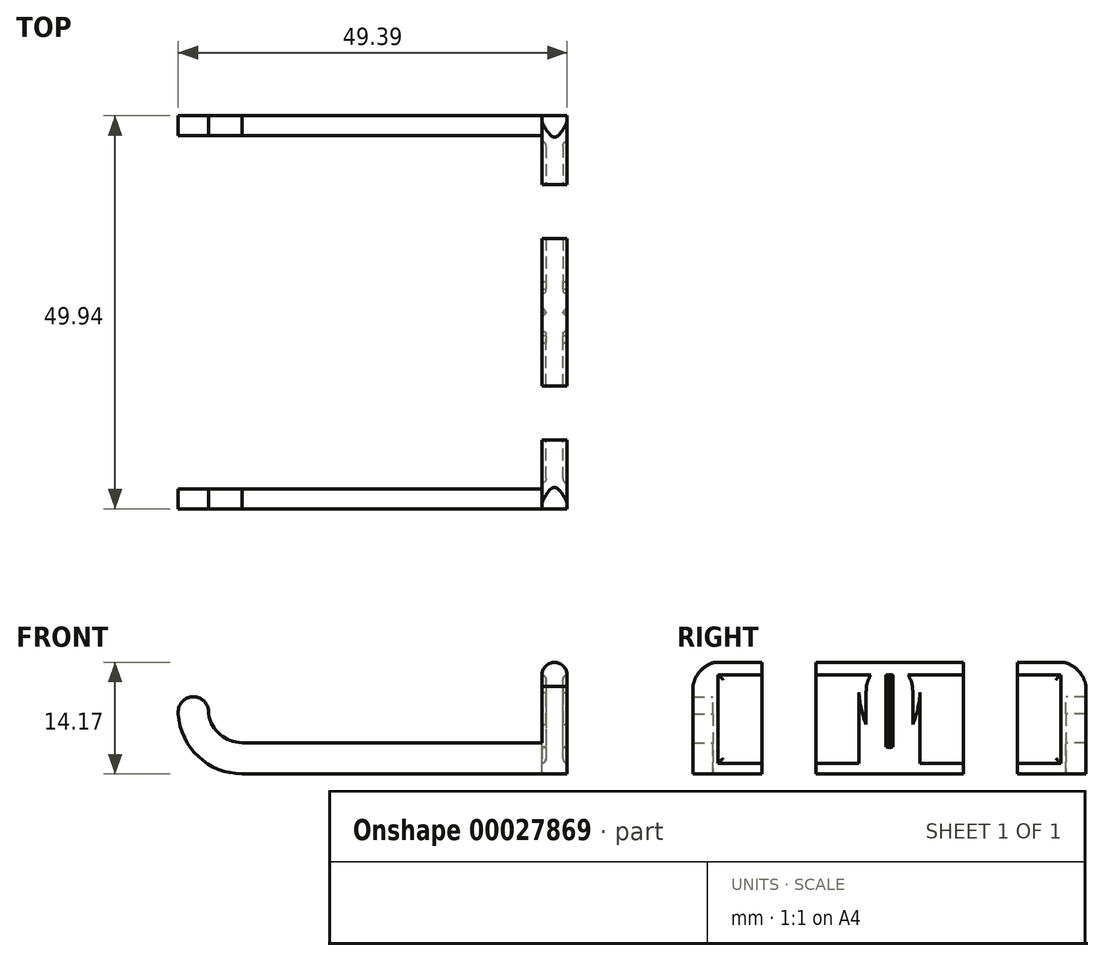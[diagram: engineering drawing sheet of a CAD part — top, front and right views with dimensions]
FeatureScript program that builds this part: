
annotation { "Feature Type Name" : "Feature", "Feature Type Description" : "" }
export const myFeature = defineFeature(function(context is Context, id is Id, definition is map)
    precondition{}
    {
        {
            var Q0;
            Q0=qCreatedBy(makeId("Front.planeOp"),FACE);
            var sketch = newSketch(context, id + "F0", { "sketchPlane" : qUnion([Q0])});
            skLineSegment(sketch, "E0", {"start": v(-12.84, 0) * mm, "end": v(25.26, 0) * mm});
            skArc(sketch, "E1", {"start": v(-20.94, 7.59) * mm, "mid": v(-18.39, 2.2) * mm, "end": v(-12.84, 0) * mm});
            skArc(sketch, "E2", {"start": v(-17.1, 7.59) * mm, "mid": v(-19.02, 9.79) * mm, "end": v(-20.94, 7.59) * mm});
            skArc(sketch, "E3", {"start": v(-17.1, 7.59) * mm, "mid": v(-15.62, 5) * mm, "end": v(-12.84, 3.94) * mm});
            skLineSegment(sketch, "E4", {"start": v(-12.84, 3.94) * mm, "end": v(25.26, 3.94) * mm});
            skLineSegment(sketch, "E5", {"start": v(25.26, 3.94) * mm, "end": v(25.26, 12.58) * mm});
            skLineSegment(sketch, "E6", {"start": v(25.26, 0) * mm, "end": v(28.43, 0) * mm});
            skLineSegment(sketch, "E7", {"start": v(28.43, 0) * mm, "end": v(28.43, 12.58) * mm});
            skArc(sketch, "E8", {"start": v(28.43, 12.58) * mm, "mid": v(26.85, 14.17) * mm, "end": v(25.26, 12.58) * mm});
            skLineSegment(sketch, "E9", {"start": v(25.26, 3.94) * mm, "end": v(25.26, 0) * mm});
            skSolve(sketch);
        }
        {
            var Q0;
            Q0=makeQuery(id+"F0.imprint","IMPRINT",FACE,{"disambiguationData":[TD([[makeQuery(id+"F0.imprint","IMPRINT",EDGE,{"derivedFrom":sQuery(id+"F0.wireOp",EDGE,"E0")}),1.0]])]});
            var Q1;
            Q1=makeQuery(id+"F0.imprint","IMPRINT",FACE,{"disambiguationData":[TD([[makeQuery(id+"F0.imprint","IMPRINT",EDGE,{"derivedFrom":sQuery(id+"F0.wireOp",EDGE,"E5")}),-1.0]])]});
            extrude(context, id + "F1", {"entities" : qUnion([Q0, Q1]), "depth" : 2.54 * mm});
        }
        {
            var Q0;
            Q0=makeQuery(id+"F0.imprint","IMPRINT",FACE,{"disambiguationData":[TD([[makeQuery(id+"F0.imprint","IMPRINT",EDGE,{"derivedFrom":sQuery(id+"F0.wireOp",EDGE,"E5")}),-1.0]])]});
            extrude(context, id + "F2", {"entities" : qUnion([Q0]), "oppositeDirection" : true, "depth" : 25.4 * mm});
        }
        {
            var Q0;
            Q0=makeQuery(id+"F2.opExtrude","SWEPT_FACE",FACE,{"disambiguationData":[OSD([sQuery(id+"F0.wireOp",EDGE,"E7")])]});
            var sketch = newSketch(context, id + "F3", { "sketchPlane" : qUnion([Q0])});
            skArc(sketch, "E10", {"start": v(1.73, 14.27) * mm, "mid": v(-1.39, 13.27) * mm, "end": v(-2.58, 10.23) * mm});
            skLineSegment(sketch, "E11", {"start": v(-2.58, 10.23) * mm, "end": v(-2.58, 14.27) * mm});
            skLineSegment(sketch, "E12", {"start": v(1.73, 14.27) * mm, "end": v(-2.58, 14.27) * mm});
            skArc(sketch, "E13.MirrorCS", {"start": v(21.09, 14.27) * mm, "mid": v(23.89, 13.54) * mm, "end": v(25.37, 11.05) * mm});
            skLineSegment(sketch, "E14.MirrorCS", {"start": v(21.09, 14.27) * mm, "end": v(25.4, 14.27) * mm});
            skLineSegment(sketch, "E15.bottom", {"start": v(0.67, 12.58) * mm, "end": v(22.89, 12.58) * mm});
            skLineSegment(sketch, "E15.top", {"start": v(0.67, 1.34) * mm, "end": v(22.89, 1.34) * mm});
            skLineSegment(sketch, "E15.right", {"start": v(22.89, 12.58) * mm, "end": v(22.89, 1.34) * mm});
            skArc(sketch, "E16", {"start": v(25.4, 12.3) * mm, "mid": v(25.4, 12.27) * mm, "end": v(25.4, 12.23) * mm});
            skPoint(sketch, "E17.orphan", {"position": v(29.58, 2) * mm});
            skLineSegment(sketch, "E18", {"start": v(25.4, 0) * mm, "end": v(29.29, 0) * mm});
            skLineSegment(sketch, "E19", {"start": v(29.29, 0) * mm, "end": v(29.29, 1.92) * mm});
            skLineSegment(sketch, "E20", {"start": v(0.67, 12.58) * mm, "end": v(0.67, 1.34) * mm});
            skLineSegment(sketch, "E21", {"start": v(25.4, 10.28) * mm, "end": v(25.4, 14.27) * mm});
            skArc(sketch, "E22.trimOffspring", {"start": v(25.37, 11.05) * mm, "mid": v(25.88, 7.57) * mm, "end": v(27.27, 4.34) * mm});
            skArc(sketch, "E23.trimOffspring", {"start": v(25.4, 10.72) * mm, "mid": v(25.4, 10.5) * mm, "end": v(25.4, 10.28) * mm});
            skArc(sketch, "E24", {"start": v(27.27, 4.34) * mm, "mid": v(28.2, 3.7) * mm, "end": v(29.29, 3.34) * mm});
            skLineSegment(sketch, "E25", {"start": v(29.29, 1.92) * mm, "end": v(29.29, 3.34) * mm});
            skPoint(sketch, "E26.start.orphan", {"position": v(29, 2) * mm});
            skSolve(sketch);
        }
        {
            var Q0;
            {var subQ0=sQuery(id+"F3.wireOp",EDGE,"E12");var subQ1=sQuery(id+"F3.wireOp",EDGE,"E10");var subQ2=makeQuery(id+"F3.imprint","INTERSECT",VERTEX,{"disambiguationData":[OD(1.0)],"derivedFrom":[subQ1,subQ0]});Q0=makeQuery(id+"F3.imprint","IMPRINT",FACE,{"disambiguationData":[TD([[makeQuery(id+"F3.imprint","IMPRINT",EDGE,{"disambiguationData":[TD([[subQ2,-1.0]])],"derivedFrom":subQ1}),-1.0]])]});}
            extrude(context, id + "F4", {"entities" : qUnion([Q0]), "operationType" : NewBodyOperationType.REMOVE, "oppositeDirection" : true, "depth" : 25.4 * mm});
        }
        {
            var Q0;
            {var subQ3=sQuery(id+"F3.wireOp",EDGE,"3297828c-8222-4a31-bb61-3fd4f8dad8b50.MirrorCS");var subQ5=sQuery(id+"F3.wireOp",EDGE,"E14.MirrorCS");var subQ6=makeQuery(id+"F3.imprint","INTERSECT",VERTEX,{"derivedFrom":[subQ5,subQ3]});Q0=makeQuery(id+"F3.imprint","IMPRINT",FACE,{"disambiguationData":[TD([[makeQuery(id+"F3.imprint","IMPRINT",EDGE,{"disambiguationData":[TD([[subQ6,1.0]])],"derivedFrom":subQ5}),-1.0]])]});}
            var Q1;
            {var subQ3=sQuery(id+"F3.wireOp",EDGE,"3297828c-8222-4a31-bb61-3fd4f8dad8b50.MirrorCS");var subQ5=sQuery(id+"F3.wireOp",EDGE,"E16");var subQ7=makeQuery(id+"F3.imprint","INTERSECT",VERTEX,{"derivedFrom":[subQ3,subQ5]});Q1=makeQuery(id+"F3.imprint","IMPRINT",FACE,{"disambiguationData":[TD([[makeQuery(id+"F3.imprint","IMPRINT",EDGE,{"disambiguationData":[TD([[subQ7,-1.0]])],"derivedFrom":subQ5}),-1.0]])]});}
            var Q2;
            {var subQ2=sQuery(id+"F3.wireOp",EDGE,"E22.trimOffspring");var subQ6=sQuery(id+"F3.wireOp",EDGE,"E13.MirrorCS");var subQ8=makeQuery(id+"F3.imprint","INTERSECT",VERTEX,{"derivedFrom":[subQ6,subQ2]});Q2=makeQuery(id+"F3.imprint","IMPRINT",FACE,{"disambiguationData":[TD([[makeQuery(id+"F3.imprint","IMPRINT",EDGE,{"disambiguationData":[TD([[subQ8,-1.0]])],"derivedFrom":subQ2}),1.0]])]});}
            extrude(context, id + "F5", {"entities" : qUnion([Q0, Q1, Q2]), "operationType" : NewBodyOperationType.REMOVE, "oppositeDirection" : true, "depth" : 25.4 * mm});
        }
        {
            var Q0;
            {var subQ5=sQuery(id+"F3.wireOp",EDGE,"E26");Q0=makeQuery(id+"F3.imprint","IMPRINT",FACE,{"disambiguationData":[TD([[makeQuery(id+"F3.imprint","IMPRINT",EDGE,{"derivedFrom":subQ5}),-1.0]])]});}
            var Q1;
            {var subQ4=sQuery(id+"F3.wireOp",EDGE,"E18");Q1=makeQuery(id+"F3.imprint","IMPRINT",FACE,{"disambiguationData":[TD([[makeQuery(id+"F3.imprint","IMPRINT",EDGE,{"derivedFrom":subQ4}),1.0]])]});}
            extrude(context, id + "F6", {"entities" : qUnion([Q0, Q1]), "oppositeDirection" : true, "depth" : 3.17 * mm});
        }
        {
            var Q0;
            Q0=makeQuery(id+"F3.imprint","IMPRINT",FACE,{"disambiguationData":[TD([[makeQuery(id+"F3.imprint","IMPRINT",EDGE,{"derivedFrom":sQuery(id+"F3.wireOp",EDGE,"E15.bottom")}),1.0]])]});
            extrude(context, id + "F7", {"entities" : qUnion([Q0]), "operationType" : NewBodyOperationType.REMOVE, "oppositeDirection" : true, "depth" : 0.5 * mm});
        }
        {
            var Q0;
            Q0=makeQuery(id+"F7.boolean.opBoolean","COPY",EDGE,{"derivedFrom":makeQuery(id+"F7.opExtrude","CAP_EDGE",EDGE,{"disambiguationData":[OSD([sQuery(id+"F3.wireOp",EDGE,"E15.bottom")])],"isStart":false})});
            var Q1;
            Q1=makeQuery(id+"F7.boolean.opBoolean","COPY",EDGE,{"derivedFrom":makeQuery(id+"F7.opExtrude","CAP_EDGE",EDGE,{"disambiguationData":[OSD([sQuery(id+"F3.wireOp",EDGE,"E15.top")])],"isStart":false})});
            var Q2;
            Q2=makeQuery(id+"F7.boolean.opBoolean","COPY",EDGE,{"derivedFrom":makeQuery(id+"F7.opExtrude","CAP_EDGE",EDGE,{"disambiguationData":[OSD([sQuery(id+"F3.wireOp",EDGE,"E15.right")])],"isStart":false})});
            var Q3;
            Q3=makeQuery(id+"F7.boolean.opBoolean","COPY",EDGE,{"derivedFrom":makeQuery(id+"F7.opExtrude","CAP_EDGE",EDGE,{"disambiguationData":[OSD([sQuery(id+"F3.wireOp",EDGE,"E20")])],"isStart":false})});
            fillet(context, id + "F8", {"entities" : qUnion([Q0, Q1, Q2, Q3]), "radius" : 0.64 * mm, "tangentPropagation" : true, "allowEdgeOverflow" : false});
        }
        {
            var Q0;
            Q0=makeQuery(id+"F2.opExtrude","SWEPT_FACE",FACE,{"disambiguationData":[OSD([sQuery(id+"F0.wireOp",EDGE,"E5"),sQuery(id+"F0.wireOp",EDGE,"E9")])]});
            var sketch = newSketch(context, id + "F9", { "sketchPlane" : qUnion([Q0])});
            skLineSegment(sketch, "E27.bottom", {"start": v(-22.9, 12.57) * mm, "end": v(-0.7, 12.57) * mm});
            skLineSegment(sketch, "E27.top", {"start": v(-22.9, 1.33) * mm, "end": v(-0.7, 1.33) * mm});
            skLineSegment(sketch, "E27.right", {"start": v(-0.7, 12.57) * mm, "end": v(-0.7, 1.33) * mm});
            skLineSegment(sketch, "E28", {"start": v(-22.9, 12.57) * mm, "end": v(-22.9, 1.33) * mm});
            skSolve(sketch);
        }
        {
            var Q0;
            Q0 = qSketchRegion(id + "F9", true);
            extrude(context, id + "F10", {"entities" : qUnion([Q0]), "operationType" : NewBodyOperationType.REMOVE, "oppositeDirection" : true, "depth" : 0.5 * mm});
        }
        {
            var Q0;
            Q0=makeQuery(id+"F10.boolean.opBoolean","COPY",EDGE,{"derivedFrom":makeQuery(id+"F10.opExtrude","CAP_EDGE",EDGE,{"disambiguationData":[OSD([sQuery(id+"F9.wireOp",EDGE,"E27.top")])],"isStart":false})});
            var Q1;
            Q1=makeQuery(id+"F10.boolean.opBoolean","COPY",EDGE,{"derivedFrom":makeQuery(id+"F10.opExtrude","CAP_EDGE",EDGE,{"disambiguationData":[OSD([sQuery(id+"F9.wireOp",EDGE,"E28")])],"isStart":false})});
            var Q2;
            Q2=makeQuery(id+"F10.boolean.opBoolean","COPY",EDGE,{"derivedFrom":makeQuery(id+"F10.opExtrude","CAP_EDGE",EDGE,{"disambiguationData":[OSD([sQuery(id+"F9.wireOp",EDGE,"E27.bottom")])],"isStart":false})});
            var Q3;
            Q3=makeQuery(id+"F10.boolean.opBoolean","COPY",EDGE,{"derivedFrom":makeQuery(id+"F10.opExtrude","CAP_EDGE",EDGE,{"disambiguationData":[OSD([sQuery(id+"F9.wireOp",EDGE,"E27.right")])],"isStart":false})});
            fillet(context, id + "F11", {"entities" : qUnion([Q0, Q1, Q2, Q3]), "radius" : 0.64 * mm, "tangentPropagation" : true, "allowEdgeOverflow" : false});
        }
        {
            var Q0;
            Q0=makeQuery(id+"F2.opExtrude","SWEPT_FACE",FACE,{"disambiguationData":[OSD([sQuery(id+"F0.wireOp",EDGE,"E7")])]});
            var sketch = newSketch(context, id + "F12", { "sketchPlane" : qUnion([Q0])});
            skLineSegment(sketch, "E29.bottom", {"start": v(6.2, -9.2) * mm, "end": v(13.06, -9.2) * mm});
            skLineSegment(sketch, "E29.top", {"start": v(6.2, 24.14) * mm, "end": v(13.06, 24.14) * mm});
            skLineSegment(sketch, "E29.left", {"start": v(6.2, -9.2) * mm, "end": v(6.2, 24.14) * mm});
            skLineSegment(sketch, "E29.right", {"start": v(13.06, -9.2) * mm, "end": v(13.06, 24.14) * mm});
            skSolve(sketch);
        }
        {
            var Q0;
            {var subQ5=sQuery(id+"F12.wireOp",EDGE,"E29.top");Q0=makeQuery(id+"F12.imprint","IMPRINT",FACE,{"disambiguationData":[TD([[makeQuery(id+"F12.imprint","IMPRINT",EDGE,{"derivedFrom":subQ5}),-1.0]])]});}
            var Q1;
            {var subQ0=sQuery(id+"F0.wireOp",EDGE,"E7");var subQ4=sQuery(id+"F12.wireOp",EDGE,"E29.left");var subQ6=makeQuery(id+"F2.opExtrude","SWEPT_EDGE",EDGE,{"disambiguationData":[OSD([sQuery(id+"F0.wireOp",EDGE,"E6"),subQ0])]});var subQ8=makeQuery(id+"F12.imprint","INTERSECT",VERTEX,{"derivedFrom":[subQ6,subQ4]});Q1=makeQuery(id+"F12.imprint","IMPRINT",FACE,{"disambiguationData":[TD([[makeQuery(id+"F12.imprint","IMPRINT",EDGE,{"disambiguationData":[TD([[subQ8,-1.0]])],"derivedFrom":subQ4}),-1.0]])]});}
            var Q2;
            {var subQ5=sQuery(id+"F12.wireOp",EDGE,"E29.bottom");Q2=makeQuery(id+"F12.imprint","IMPRINT",FACE,{"disambiguationData":[TD([[makeQuery(id+"F12.imprint","IMPRINT",EDGE,{"derivedFrom":subQ5}),1.0]])]});}
            extrude(context, id + "F13", {"entities" : qUnion([Q0, Q1, Q2]), "operationType" : NewBodyOperationType.REMOVE, "oppositeDirection" : true, "depth" : 50.8 * mm});
        }
        {
            var Q0;
            Q0=makeQuery(id+"F1.opExtrude","SWEPT_BODY",BODY,{"disambiguationData":[OSD([sQuery(id+"F0.wireOp",EDGE,"E0"),sQuery(id+"F0.wireOp",EDGE,"E1"),sQuery(id+"F0.wireOp",EDGE,"E2"),sQuery(id+"F0.wireOp",EDGE,"E3"),sQuery(id+"F0.wireOp",EDGE,"E4"),sQuery(id+"F0.wireOp",EDGE,"E5"),sQuery(id+"F0.wireOp",EDGE,"E6"),sQuery(id+"F0.wireOp",EDGE,"E7"),sQuery(id+"F0.wireOp",EDGE,"E8")])]});
            var Q1;
            Q1=makeQuery(id+"F13.boolean.opBoolean","SPLIT",BODY,{"disambiguationData":[OD(0.0)],"derivedFrom":makeQuery(id+"F2.opExtrude","SWEPT_BODY",BODY,{"disambiguationData":[OSD([sQuery(id+"F0.wireOp",EDGE,"E5"),sQuery(id+"F0.wireOp",EDGE,"E6"),sQuery(id+"F0.wireOp",EDGE,"E7"),sQuery(id+"F0.wireOp",EDGE,"E8"),sQuery(id+"F0.wireOp",EDGE,"E9")])]})});
            transform(context, id + "F14", {"entities" : qUnion([Q0, Q1]), "transformType" : TransformType.TRANSLATION_3D, "dx" : 0 * mm, "dy" : 6.86 * mm, "dz" : 0 * mm, "makeCopy" : false});
        }
        {
            var Q0;
            Q0=makeQuery(id+"F13.boolean.opBoolean","SPLIT",BODY,{"disambiguationData":[OD(1.0)],"derivedFrom":makeQuery(id+"F2.opExtrude","SWEPT_BODY",BODY,{"disambiguationData":[OSD([sQuery(id+"F0.wireOp",EDGE,"E5"),sQuery(id+"F0.wireOp",EDGE,"E6"),sQuery(id+"F0.wireOp",EDGE,"E7"),sQuery(id+"F0.wireOp",EDGE,"E8"),sQuery(id+"F0.wireOp",EDGE,"E9")])]})});
            var Q1;
            Q1=makeQuery(id+"F1.opExtrude","SWEPT_BODY",BODY,{"disambiguationData":[OSD([sQuery(id+"F0.wireOp",EDGE,"E0"),sQuery(id+"F0.wireOp",EDGE,"E1"),sQuery(id+"F0.wireOp",EDGE,"E2"),sQuery(id+"F0.wireOp",EDGE,"E3"),sQuery(id+"F0.wireOp",EDGE,"E4"),sQuery(id+"F0.wireOp",EDGE,"E5"),sQuery(id+"F0.wireOp",EDGE,"E6"),sQuery(id+"F0.wireOp",EDGE,"E7"),sQuery(id+"F0.wireOp",EDGE,"E8")])]});
            var Q2;
            Q2=makeQuery(id+"F13.boolean.opBoolean","SPLIT",BODY,{"disambiguationData":[OD(0.0)],"derivedFrom":makeQuery(id+"F2.opExtrude","SWEPT_BODY",BODY,{"disambiguationData":[OSD([sQuery(id+"F0.wireOp",EDGE,"E5"),sQuery(id+"F0.wireOp",EDGE,"E6"),sQuery(id+"F0.wireOp",EDGE,"E7"),sQuery(id+"F0.wireOp",EDGE,"E8"),sQuery(id+"F0.wireOp",EDGE,"E9")])]})});
            var Q3;
            Q3=makeQuery(id+"F6.opExtrude","SWEPT_BODY",BODY,{"disambiguationData":[OSD([sQuery(id+"F0.wireOp",EDGE,"E7"),sQuery(id+"F3.wireOp",EDGE,"E18"),sQuery(id+"F3.wireOp",EDGE,"E19"),sQuery(id+"F3.wireOp",EDGE,"E22.trimOffspring"),sQuery(id+"F3.wireOp",EDGE,"E24"),sQuery(id+"F3.wireOp",EDGE,"E25")])]});
            var Q4;
            Q4=makeQuery(id+"F6.opExtrude","SWEPT_FACE",FACE,{"disambiguationData":[OSD([sQuery(id+"F3.wireOp",EDGE,"E19"),sQuery(id+"F3.wireOp",EDGE,"E25")])]});
            mirror(context, id + "F15", {"operationType" : NewBodyOperationType.ADD, "entities" : qUnion([Q0, Q1, Q2, Q3]), "mirrorPlane" : qUnion([Q4])});
        }
    });
